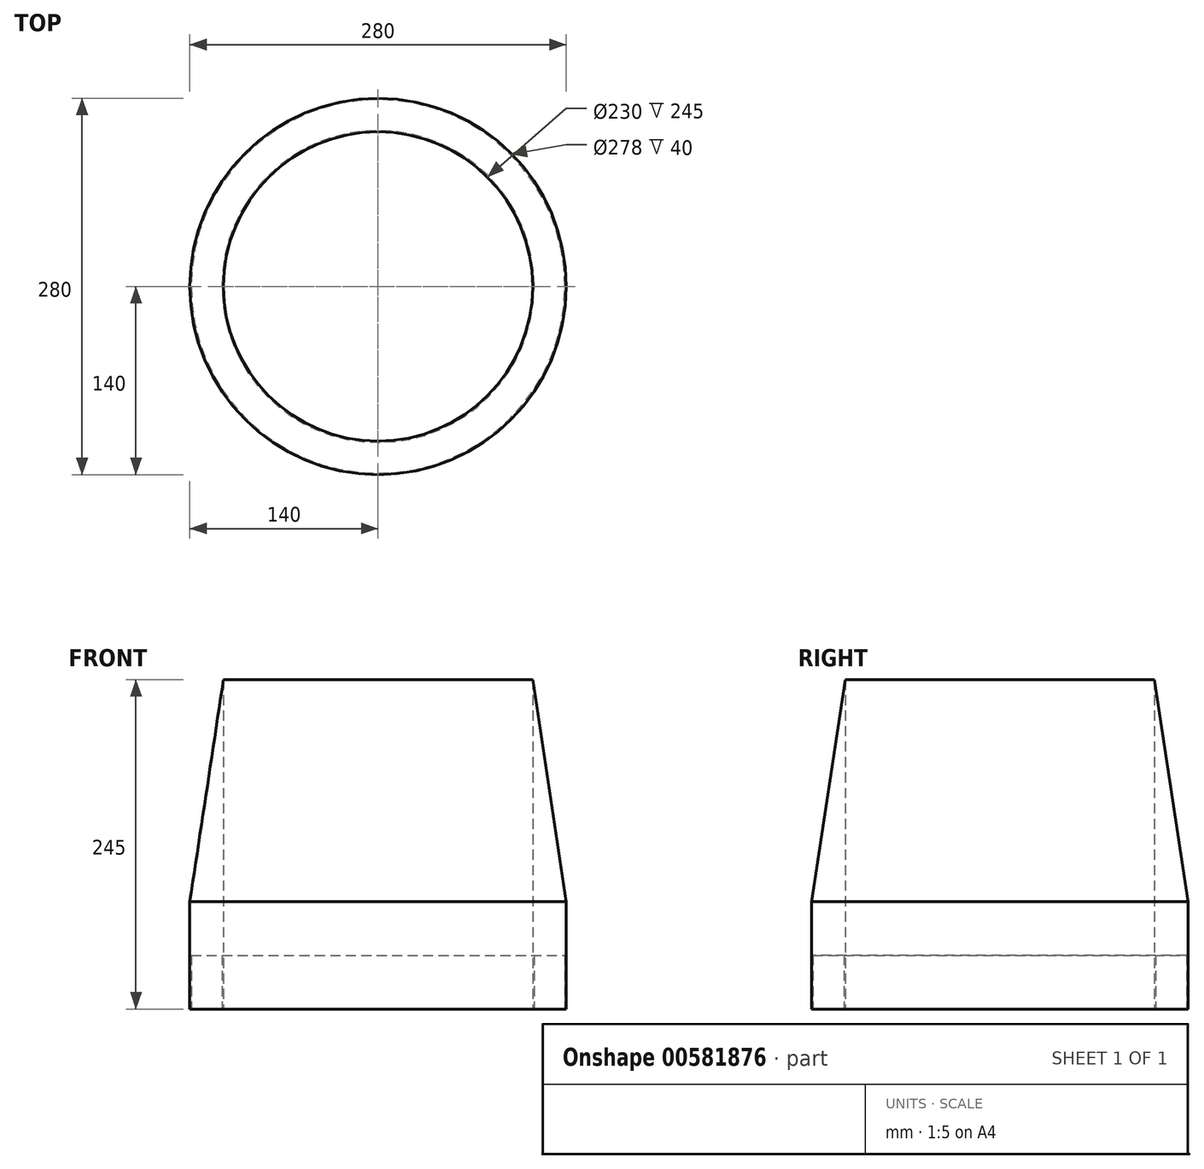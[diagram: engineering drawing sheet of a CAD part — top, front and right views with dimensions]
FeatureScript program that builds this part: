
annotation { "Feature Type Name" : "Feature", "Feature Type Description" : "" }
export const myFeature = defineFeature(function(context is Context, id is Id, definition is map)
    precondition{}
    {
        {
            var Q0;
            Q0=qCreatedBy(makeId("Front.planeOp"),FACE);
            var sketch = newSketch(context, id + "F0", { "sketchPlane" : qUnion([Q0])});
            skLineSegment(sketch, "E0", {"start": v(0, -139.25) * mm, "end": v(0, 240.83) * mm, "construction": true});
            skLineSegment(sketch, "E1", {"start": v(-115, -67.22) * mm, "end": v(-115, 177.78) * mm});
            skLineSegment(sketch, "E2", {"start": v(-115, 177.78) * mm, "end": v(-140, 12.78) * mm});
            skLineSegment(sketch, "E3", {"start": v(-140, 12.78) * mm, "end": v(-140, -67.22) * mm});
            skLineSegment(sketch, "E4", {"start": v(-140, -67.22) * mm, "end": v(-139, -67.22) * mm});
            skLineSegment(sketch, "E5", {"start": v(-139, -67.22) * mm, "end": v(-139, -27.22) * mm});
            skLineSegment(sketch, "E6", {"start": v(-139, -27.22) * mm, "end": v(-116, -27.22) * mm});
            skLineSegment(sketch, "E7", {"start": v(-116, -27.22) * mm, "end": v(-116, -67.22) * mm});
            skLineSegment(sketch, "E8", {"start": v(-116, -67.22) * mm, "end": v(-115, -67.22) * mm});
            skSolve(sketch);
        }
        {
            var Q0;
            Q0=qSketchRegion(id+"F0",true);
            var Q1;
            Q1=sQuery(id+"F0.wireOp",EDGE,"E0");
            revolve(context, id + "F1", {"entities" : qUnion([Q0]), "axis" : qUnion([Q1]), "revolveType" : RevolveType.FULL});
        }
    });
